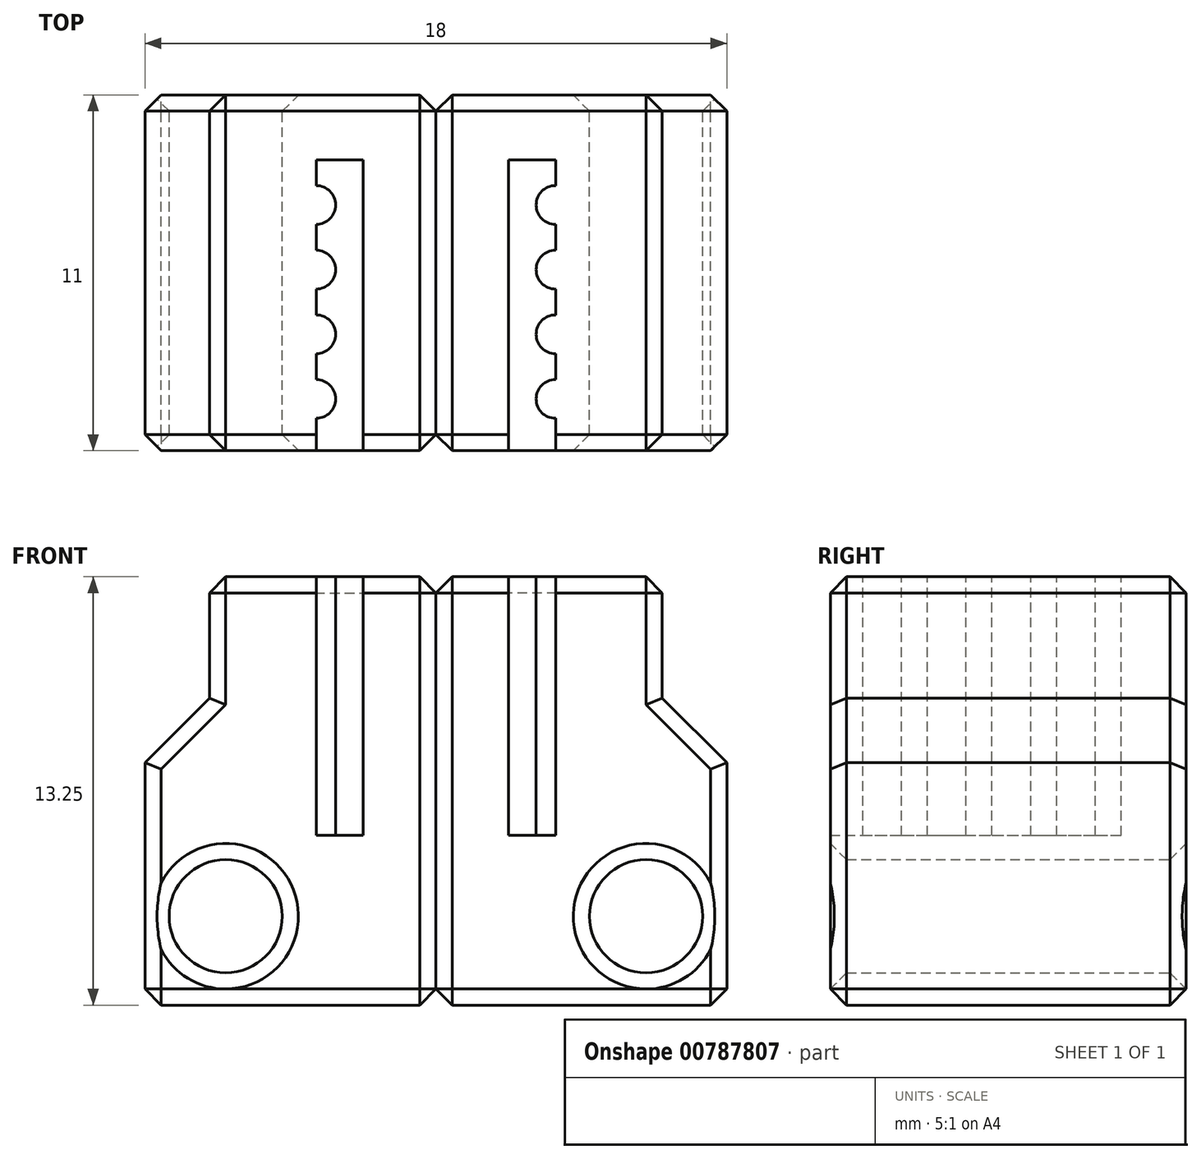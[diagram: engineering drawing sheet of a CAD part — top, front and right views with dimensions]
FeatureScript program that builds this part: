
annotation { "Feature Type Name" : "Feature", "Feature Type Description" : "" }
export const myFeature = defineFeature(function(context is Context, id is Id, definition is map)
    precondition{}
    {
        {
            var Q0;
            Q0=qCreatedBy(makeId("Front.planeOp"),FACE);
            var sketch = newSketch(context, id + "F0", { "sketchPlane" : qUnion([Q0])});
            skLineSegment(sketch, "E0", {"start": v(0, 0) * mm, "end": v(0, 13.25) * mm});
            skLineSegment(sketch, "E1", {"start": v(0, 13.25) * mm, "end": v(-7, 13.25) * mm});
            skLineSegment(sketch, "E2", {"start": v(-7, 13.25) * mm, "end": v(-7, 9.5) * mm});
            skLineSegment(sketch, "E3", {"start": v(-7, 9.5) * mm, "end": v(-9, 7.5) * mm});
            skLineSegment(sketch, "E4", {"start": v(-9, 7.5) * mm, "end": v(-9, 0) * mm});
            skLineSegment(sketch, "E5", {"start": v(-9, 0) * mm, "end": v(0, 0) * mm});
            skCircle(sketch, "E6", {"center": v(-6.5, 2.75) * mm, "radius": 1.75 * mm});
            skSolve(sketch);
        }
        {
            var Q0;
            Q0=makeQuery(id+"F0.imprint","IMPRINT",FACE,{"disambiguationData":[TD([[makeQuery(id+"F0.imprint","IMPRINT",EDGE,{"derivedFrom":sQuery(id+"F0.wireOp",EDGE,"E0")}),1.0]])]});
            extrude(context, id + "F1", {"entities" : qUnion([Q0]), "depth" : 11 * mm, "offsetDistance" : 25 * mm});
        }
        {
            var Q0;
            Q0=makeQuery(id+"F1.opExtrude","SWEPT_FACE",FACE,{"disambiguationData":[OSD([sQuery(id+"F0.wireOp",EDGE,"E1")])]});
            var sketch = newSketch(context, id + "F2", { "sketchPlane" : qUnion([Q0])});
            skLineSegment(sketch, "E7.bottom", {"start": v(-2.25, -11) * mm, "end": v(-3.7, -11) * mm});
            skLineSegment(sketch, "E7.top", {"start": v(-2.25, -2) * mm, "end": v(-3.7, -2) * mm});
            skLineSegment(sketch, "E7.left", {"start": v(-2.25, -11) * mm, "end": v(-2.25, -2) * mm});
            skLineSegment(sketch, "E7.right", {"start": v(-3.7, -11) * mm, "end": v(-3.7, -2) * mm});
            skCircle(sketch, "E8", {"center": v(-3.7, -9.4) * mm, "radius": 0.6 * mm});
            skCircle(sketch, "E9", {"center": v(-3.7, -7.4) * mm, "radius": 0.6 * mm});
            skCircle(sketch, "E10", {"center": v(-3.7, -5.4) * mm, "radius": 0.6 * mm});
            skCircle(sketch, "E11", {"center": v(-3.7, -3.4) * mm, "radius": 0.6 * mm});
            skSolve(sketch);
        }
        {
            var Q0;
            {var subQ13=sQuery(id+"F2.wireOp",EDGE,"E7.bottom");Q0=makeQuery(id+"F2.imprint","IMPRINT",FACE,{"disambiguationData":[TD([[makeQuery(id+"F2.imprint","IMPRINT",EDGE,{"derivedFrom":subQ13}),-1.0]])]});}
            extrude(context, id + "F3", {"entities" : qUnion([Q0]), "operationType" : NewBodyOperationType.REMOVE, "oppositeDirection" : true, "depth" : 8 * mm, "offsetDistance" : 25 * mm});
        }
        {
            var Q0;
            Q0=makeQuery(id+"F1.opExtrude","CAP_EDGE",EDGE,{"disambiguationData":[OSD([sQuery(id+"F0.wireOp",EDGE,"E5")])],"isStart":true});
            var Q1;
            Q1=makeQuery(id+"F1.opExtrude","CAP_EDGE",EDGE,{"disambiguationData":[OSD([sQuery(id+"F0.wireOp",EDGE,"E0")])],"isStart":true});
            var Q2;
            Q2=makeQuery(id+"F1.opExtrude","CAP_EDGE",EDGE,{"disambiguationData":[OSD([sQuery(id+"F0.wireOp",EDGE,"E2")])],"isStart":true});
            var Q3;
            Q3=makeQuery(id+"F1.opExtrude","CAP_EDGE",EDGE,{"disambiguationData":[OSD([sQuery(id+"F0.wireOp",EDGE,"E3")])],"isStart":true});
            var Q4;
            Q4=makeQuery(id+"F1.opExtrude","CAP_EDGE",EDGE,{"disambiguationData":[OSD([sQuery(id+"F0.wireOp",EDGE,"E4")])],"isStart":true});
            var Q5;
            Q5=makeQuery(id+"F1.opExtrude","SWEPT_EDGE",EDGE,{"disambiguationData":[OSD([sQuery(id+"F0.wireOp",EDGE,"E4"),sQuery(id+"F0.wireOp",EDGE,"E5")])]});
            var Q6;
            Q6=makeQuery(id+"F1.opExtrude","CAP_EDGE",EDGE,{"disambiguationData":[OSD([sQuery(id+"F0.wireOp",EDGE,"E4")])],"isStart":false});
            var Q7;
            Q7=makeQuery(id+"F1.opExtrude","CAP_EDGE",EDGE,{"disambiguationData":[OSD([sQuery(id+"F0.wireOp",EDGE,"E3")])],"isStart":false});
            var Q8;
            Q8=makeQuery(id+"F1.opExtrude","CAP_EDGE",EDGE,{"disambiguationData":[OSD([sQuery(id+"F0.wireOp",EDGE,"E2")])],"isStart":false});
            var Q9;
            Q9=makeQuery(id+"F1.opExtrude","CAP_EDGE",EDGE,{"disambiguationData":[OSD([sQuery(id+"F0.wireOp",EDGE,"E5")])],"isStart":false});
            var Q10;
            Q10=makeQuery(id+"F1.opExtrude","CAP_EDGE",EDGE,{"disambiguationData":[OSD([sQuery(id+"F0.wireOp",EDGE,"E0")])],"isStart":false});
            var Q11;
            Q11=makeQuery(id+"F1.opExtrude","SWEPT_EDGE",EDGE,{"disambiguationData":[OSD([sQuery(id+"F0.wireOp",EDGE,"E0"),sQuery(id+"F0.wireOp",EDGE,"E5")])]});
            var Q12;
            Q12=makeQuery(id+"F1.opExtrude","SWEPT_EDGE",EDGE,{"disambiguationData":[OSD([sQuery(id+"F0.wireOp",EDGE,"E0"),sQuery(id+"F0.wireOp",EDGE,"E1")])]});
            var Q13;
            Q13=makeQuery(id+"F1.opExtrude","SWEPT_EDGE",EDGE,{"disambiguationData":[OSD([sQuery(id+"F0.wireOp",EDGE,"E1"),sQuery(id+"F0.wireOp",EDGE,"E2")])]});
            var Q14;
            Q14=makeQuery(id+"F1.opExtrude","CAP_EDGE",EDGE,{"disambiguationData":[OSD([sQuery(id+"F0.wireOp",EDGE,"E1")])],"isStart":true});
            var Q15;
            {var subQ0=sQuery(id+"F0.wireOp",EDGE,"E0");var subQ1=sQuery(id+"F0.wireOp",EDGE,"E1");Q15=makeQuery(id+"F3.boolean.opBoolean","SPLIT",EDGE,{"disambiguationData":[TD([makeQuery(id+"F1.opExtrude","SWEPT_FACE",FACE,{"disambiguationData":[OSD([subQ0])]})])],"derivedFrom":makeQuery(id+"F1.opExtrude","CAP_EDGE",EDGE,{"disambiguationData":[OSD([subQ1])],"isStart":false})});}
            var Q16;
            {var subQ0=sQuery(id+"F0.wireOp",EDGE,"E2");var subQ1=sQuery(id+"F0.wireOp",EDGE,"E1");var subQ3=makeQuery(id+"F1.opExtrude","CAP_EDGE",EDGE,{"disambiguationData":[OSD([subQ1])],"isStart":false});Q16=makeQuery(id+"F3.boolean.opBoolean","SPLIT",EDGE,{"disambiguationData":[TD([makeQuery(id+"F1.opExtrude","SWEPT_FACE",FACE,{"disambiguationData":[OSD([subQ0])]})])],"derivedFrom":subQ3});}
            var Q17;
            Q17=makeQuery(id+"F1.opExtrude","CAP_EDGE",EDGE,{"disambiguationData":[OSD([sQuery(id+"F0.wireOp",EDGE,"E6")])],"isStart":true});
            var Q18;
            Q18=makeQuery(id+"F1.opExtrude","CAP_EDGE",EDGE,{"disambiguationData":[OSD([sQuery(id+"F0.wireOp",EDGE,"E6")])],"isStart":false});
            chamfer(context, id + "F4", {"entities" : qUnion([Q0, Q1, Q2, Q3, Q4, Q5, Q6, Q7, Q8, Q9, Q10, Q11, Q12, Q13, Q14, Q15, Q16, Q17, Q18]), "width" : 0.5 * mm, "tangentPropagation" : true});
        }
        {
            var Q0;
            Q0=makeQuery(id+"F1.opExtrude","SWEPT_BODY",BODY,{"disambiguationData":[OSD([sQuery(id+"F0.wireOp",EDGE,"E0"),sQuery(id+"F0.wireOp",EDGE,"E1"),sQuery(id+"F0.wireOp",EDGE,"E2"),sQuery(id+"F0.wireOp",EDGE,"E3"),sQuery(id+"F0.wireOp",EDGE,"E4"),sQuery(id+"F0.wireOp",EDGE,"E5"),sQuery(id+"F0.wireOp",EDGE,"E6")])]});
            var Q1;
            Q1=qCreatedBy(makeId("Right.planeOp"),FACE);
            mirror(context, id + "F5", {"entities" : qUnion([Q0]), "mirrorPlane" : qUnion([Q1])});
        }
    });
